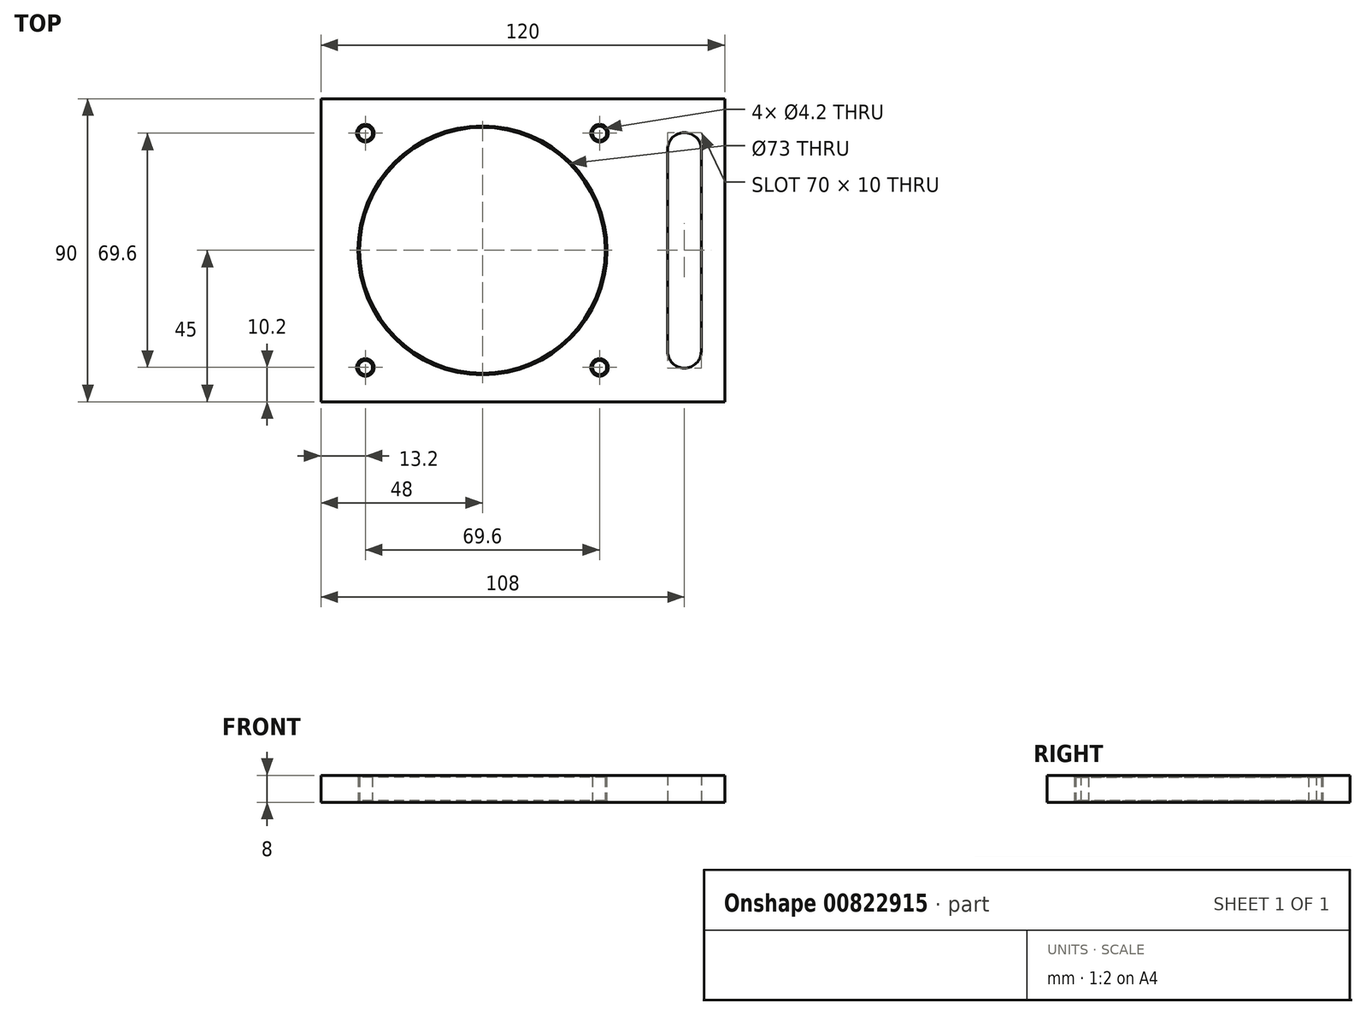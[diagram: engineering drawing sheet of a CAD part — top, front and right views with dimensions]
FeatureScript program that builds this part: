
annotation { "Feature Type Name" : "Feature", "Feature Type Description" : "" }
export const myFeature = defineFeature(function(context is Context, id is Id, definition is map)
    precondition{}
    {
        {
            var Q0;
            Q0=qCreatedBy(makeId("Top.planeOp"),FACE);
            var sketch = newSketch(context, id + "F0", { "sketchPlane" : qUnion([Q0])});
            skLineSegment(sketch, "E0.bottom", {"start": v(-12, 142.5) * mm, "end": v(12, 142.5) * mm, "construction": true});
            skLineSegment(sketch, "E0.top", {"start": v(-12, -142.5) * mm, "end": v(12, -142.5) * mm, "construction": true});
            skLineSegment(sketch, "E0.left", {"start": v(-12, 142.5) * mm, "end": v(-12, -142.5) * mm, "construction": true});
            skLineSegment(sketch, "E0.right", {"start": v(12, 142.5) * mm, "end": v(12, -142.5) * mm, "construction": true});
            skPoint(sketch, "E0.middle", {"position": v(0, 0) * mm});
            skLineSegment(sketch, "E1", {"start": v(0, 0) * mm, "end": v(36, 0) * mm, "construction": true});
            skLineSegment(sketch, "E2", {"start": v(0, 0) * mm, "end": v(-84, 0) * mm, "construction": true});
            skCircle(sketch, "E3", {"center": v(-84, 0) * mm, "radius": 25.46 * mm, "construction": true});
            skCircle(sketch, "E4", {"center": v(36, 0) * mm, "radius": 25.46 * mm, "construction": true});
            skCircle(sketch, "E5", {"center": v(-84, 0) * mm, "radius": 36.5 * mm});
            skLineSegment(sketch, "E6.bottom", {"start": v(-127.5, -43.5) * mm, "end": v(-40.5, -43.5) * mm, "construction": true});
            skLineSegment(sketch, "E6.top", {"start": v(-127.5, 43.5) * mm, "end": v(-40.5, 43.5) * mm, "construction": true});
            skLineSegment(sketch, "E6.left", {"start": v(-127.5, -43.5) * mm, "end": v(-127.5, 43.5) * mm, "construction": true});
            skLineSegment(sketch, "E6.right", {"start": v(-40.5, -43.5) * mm, "end": v(-40.5, 43.5) * mm, "construction": true});
            skLineSegment(sketch, "E7.bottom", {"start": v(-132, 45) * mm, "end": v(-36, 45) * mm, "construction": true});
            skLineSegment(sketch, "E7.top", {"start": v(-132, -45) * mm, "end": v(-36, -45) * mm, "construction": true});
            skLineSegment(sketch, "E7.left", {"start": v(-132, 45) * mm, "end": v(-132, -45) * mm});
            skLineSegment(sketch, "E7.right", {"start": v(-36, 45) * mm, "end": v(-36, -45) * mm, "construction": true});
            skLineSegment(sketch, "E8", {"start": v(-12, 0) * mm, "end": v(-12, 45) * mm});
            skLineSegment(sketch, "E9", {"start": v(-12, 45) * mm, "end": v(-37, 45) * mm});
            skLineSegment(sketch, "E10", {"start": v(-37, 45) * mm, "end": v(-132, 45) * mm});
            skLineSegment(sketch, "E11.MirrorCS", {"start": v(-37, -45) * mm, "end": v(-132, -45) * mm});
            skLineSegment(sketch, "E12.MirrorCS", {"start": v(-12, 0) * mm, "end": v(-12, -45) * mm});
            skLineSegment(sketch, "E13.MirrorCS", {"start": v(-12, -45) * mm, "end": v(-37, -45) * mm});
            skLineSegment(sketch, "E14.bottom", {"start": v(-118.8, -34.8) * mm, "end": v(-49.2, -34.8) * mm, "construction": true});
            skLineSegment(sketch, "E14.top", {"start": v(-118.8, 34.8) * mm, "end": v(-49.2, 34.8) * mm, "construction": true});
            skLineSegment(sketch, "E14.left", {"start": v(-118.8, -34.8) * mm, "end": v(-118.8, 34.8) * mm, "construction": true});
            skLineSegment(sketch, "E14.right", {"start": v(-49.2, -34.8) * mm, "end": v(-49.2, 34.8) * mm, "construction": true});
            skCircle(sketch, "E15", {"center": v(-118.8, 34.8) * mm, "radius": 2.1 * mm});
            skCircle(sketch, "E16", {"center": v(-49.2, 34.8) * mm, "radius": 2.1 * mm});
            skCircle(sketch, "E17", {"center": v(-49.2, -34.8) * mm, "radius": 2.1 * mm});
            skCircle(sketch, "E18", {"center": v(-118.8, -34.8) * mm, "radius": 2.1 * mm});
            skArc(sketch, "E19", {"start": v(-19, 30) * mm, "mid": v(-24, 35) * mm, "end": v(-29, 30) * mm});
            skArc(sketch, "E20.MirrorC", {"start": v(-19, -30) * mm, "mid": v(-24, -35) * mm, "end": v(-29, -30) * mm});
            skLineSegment(sketch, "E21", {"start": v(-24, -30) * mm, "end": v(-29, -30) * mm, "construction": true});
            skLineSegment(sketch, "E22", {"start": v(-29, -30) * mm, "end": v(-29, 30) * mm});
            skLineSegment(sketch, "E23", {"start": v(-29, 30) * mm, "end": v(-19, 30) * mm, "construction": true});
            skLineSegment(sketch, "E24", {"start": v(-19, 30) * mm, "end": v(-19, -30) * mm});
            skLineSegment(sketch, "E25", {"start": v(-19, -30) * mm, "end": v(-24, -30) * mm, "construction": true});
            skSolve(sketch);
        }
        {
            var Q0;
            Q0=qSketchRegion(id+"F0",true);
            extrude(context, id + "F1", {"entities" : qUnion([Q0]), "depth" : 8 * mm, "offsetDistance" : 25 * mm});
        }
        {
            var Q0;
            Q0=makeQuery(id+"F1.opExtrude","SWEPT_FACE",FACE,{"disambiguationData":[OSD([sQuery(id+"F0.wireOp",EDGE,"E5")])]});
            var Q1;
            Q1=makeQuery(id+"F1.opExtrude","SWEPT_FACE",FACE,{"disambiguationData":[OSD([sQuery(id+"F0.wireOp",EDGE,"E18")])]});
            var Q2;
            Q2=makeQuery(id+"F1.opExtrude","SWEPT_FACE",FACE,{"disambiguationData":[OSD([sQuery(id+"F0.wireOp",EDGE,"E15")])]});
            var Q3;
            Q3=makeQuery(id+"F1.opExtrude","SWEPT_FACE",FACE,{"disambiguationData":[OSD([sQuery(id+"F0.wireOp",EDGE,"E16")])]});
            var Q4;
            Q4=makeQuery(id+"F1.opExtrude","SWEPT_FACE",FACE,{"disambiguationData":[OSD([sQuery(id+"F0.wireOp",EDGE,"E17")])]});
            chamfer(context, id + "F2", {"entities" : qUnion([Q0, Q1, Q2, Q3, Q4]), "width" : 0.5 * mm, "tangentPropagation" : true});
        }
    });
